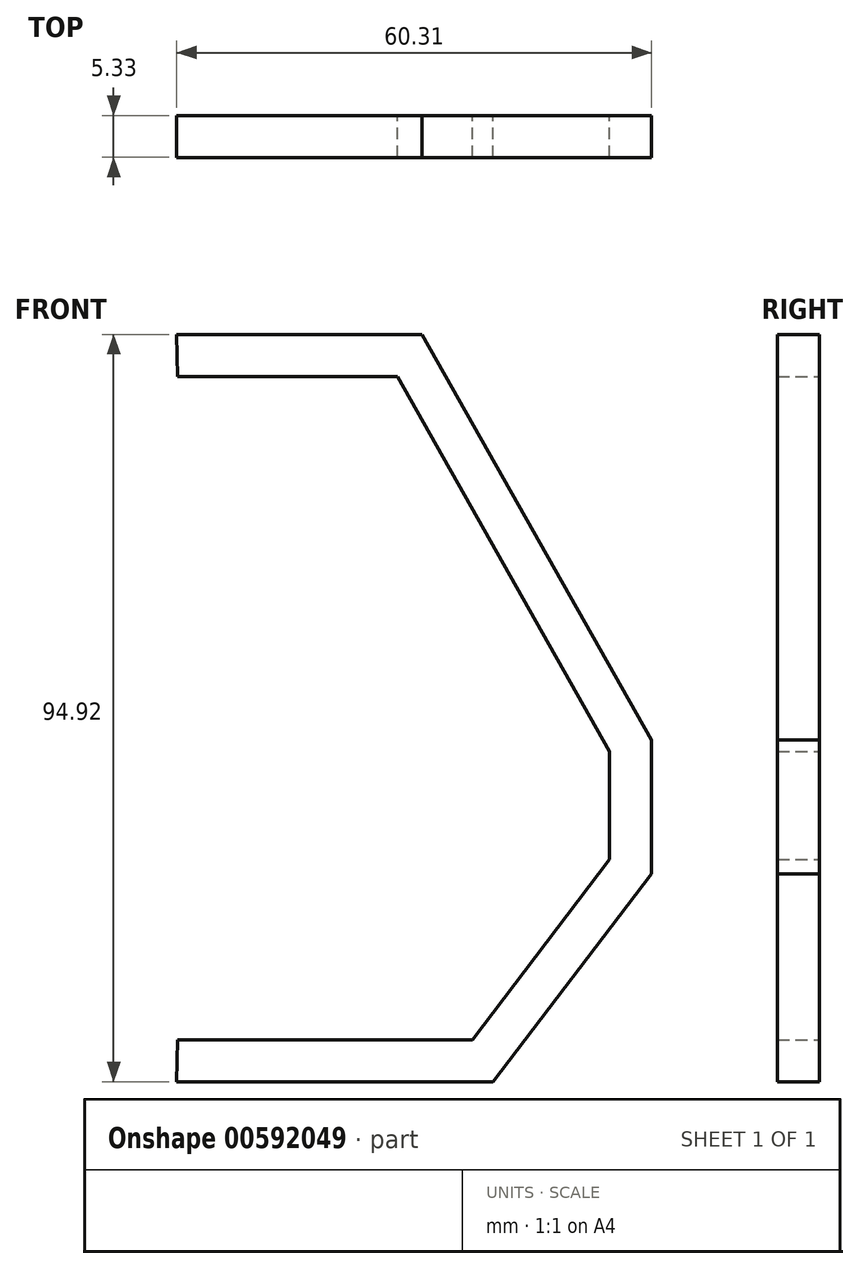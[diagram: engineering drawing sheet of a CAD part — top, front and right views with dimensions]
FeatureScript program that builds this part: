
annotation { "Feature Type Name" : "Feature", "Feature Type Description" : "" }
export const myFeature = defineFeature(function(context is Context, id is Id, definition is map)
    precondition{}
    {
        {
            var Q0;
            Q0=qCreatedBy(makeId("Front.planeOp"),FACE);
            var sketch = newSketch(context, id + "F0", { "sketchPlane" : qUnion([Q0])});
            skLineSegment(sketch, "E0", {"start": v(0, 51.54) * mm, "end": v(31.15, 51.54) * mm});
            skLineSegment(sketch, "E1", {"start": v(31.15, 51.54) * mm, "end": v(60.3, 0) * mm});
            skLineSegment(sketch, "E2", {"start": v(60.3, 0) * mm, "end": v(60.3, -16.97) * mm});
            skLineSegment(sketch, "E3", {"start": v(60.3, -16.97) * mm, "end": v(40.2, -43.38) * mm});
            skLineSegment(sketch, "E4", {"start": v(40.2, -43.38) * mm, "end": v(0, -43.38) * mm});
            skLineSegment(sketch, "E5.0", {"start": v(37.55, -38.05) * mm, "end": v(0.08, -38.05) * mm});
            skLineSegment(sketch, "E5.1", {"start": v(0.07, 46.21) * mm, "end": v(28.04, 46.21) * mm});
            skLineSegment(sketch, "E5.2", {"start": v(28.04, 46.21) * mm, "end": v(54.97, -1.4) * mm});
            skLineSegment(sketch, "E5.3", {"start": v(54.97, -1.4) * mm, "end": v(54.97, -15.17) * mm});
            skLineSegment(sketch, "E5.4", {"start": v(54.97, -15.17) * mm, "end": v(37.55, -38.05) * mm});
            skLineSegment(sketch, "E6", {"start": v(0, 51.54) * mm, "end": v(0.07, 46.21) * mm});
            skLineSegment(sketch, "E7", {"start": v(0.08, -38.05) * mm, "end": v(0, -43.38) * mm});
            skSolve(sketch);
        }
        {
            var Q0;
            Q0 = qSketchRegion(id + "F0", true);
            extrude(context, id + "F1", {"entities" : qUnion([Q0]), "depth" : 5.33 * mm, "offsetDistance" : 25.4 * mm});
        }
    });
